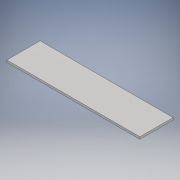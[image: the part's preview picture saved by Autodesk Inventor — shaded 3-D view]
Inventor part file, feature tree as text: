
AUTODESK INVENTOR PART (.ipt)
format: ipt  version: 2017 (Build 210142000, 142)  size: 92,160 bytes
history: native  units: mm
features: extrude x1, sketch x1
ambient origin geometry x8: Origin, YZ Plane, XZ Plane, XY Plane, X Axis, Y Axis, Z Axis, Center Point
bodies: Body1 (feature_tree)
feature tree (2):
  extrude  "Extrusion2"  Depth=94.0mm
  sketch  "Sketch1"  dims[d0=375.92mm d1=94.0mm d4=6.0mm d5=0.0mm]
